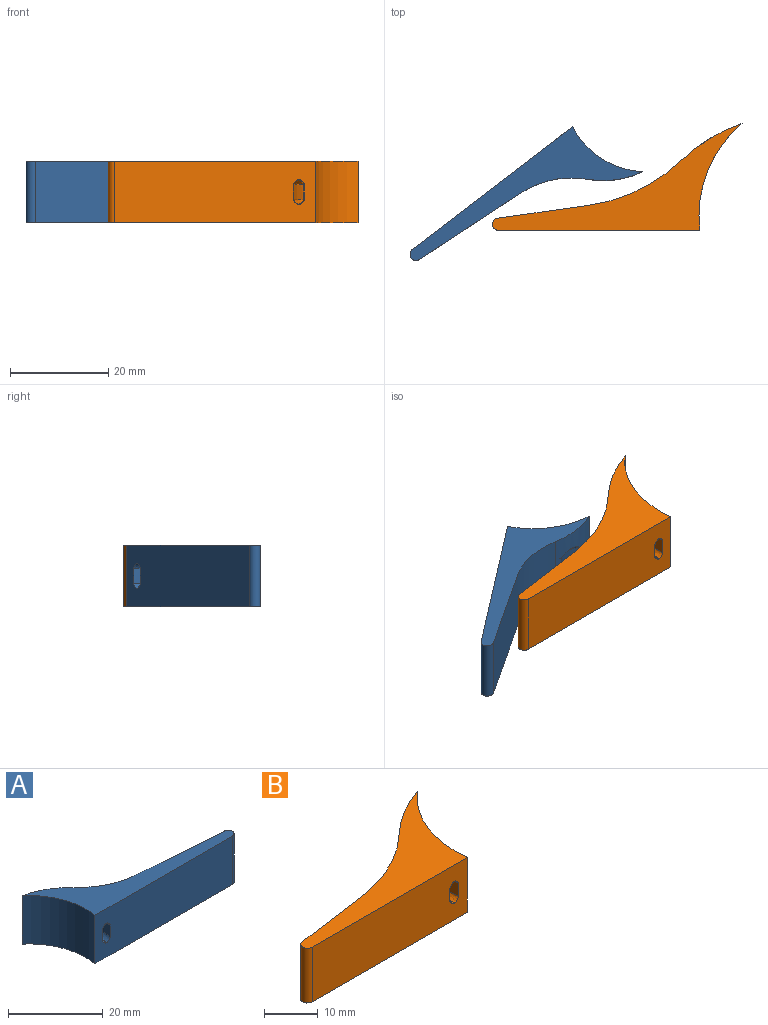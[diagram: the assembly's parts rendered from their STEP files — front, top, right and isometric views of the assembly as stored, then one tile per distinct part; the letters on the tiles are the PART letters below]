
ASSEMBLY  parts=2 mates=1
PART A: 16 faces, bbox 48.3x17.1x12.7 mm
  f0: plane 41.22x12.71mm, normal (0,-1,0), area 502.6mm2, adj f2,f3,f6,f7,f8,f9,f10,f11
  f1: cylinder r=18.88mm len=12.5mm, axis (0,0,1), area 123.5mm2, adj f2,f5,f6,f7,f8,f9,f10,f11
  f2: cylinder r=17mm len=15.97mm, axis (0,0,1), area 222.5mm2, adj f0,f1,f6,f7
  f3: cylinder r=1.24mm len=12.5mm, axis (0,0,1), area 47.6mm2, adj f0,f4,f6,f7
  f4: plane 24.55x12.5mm, normal (0.07,1,0), area 307.7mm2, adj f3,f5,f6,f7
  f5: cylinder r=18.88mm len=12.5mm, axis (0,0,1), area 177.2mm2, adj f1,f4,f6,f7
  f6: plane 48.06x15.97mm, normal (0,0,1), area 228.8mm2, adj f0,f1,f2,f3,f4,f5
  f7: plane 48.06x15.97mm, normal (0,0,-1), area 228.8mm2, adj f0,f1,f2,f3,f4,f5
  f8: plane 13.24x3.15mm, normal (0,0,1), area 3.1mm2, adj f0,f1,f14,f15
  f9: cylinder r=21.47mm len=11.42mm, axis (0,0,-1), area 35mm2, adj f0,f1,f13,f15
  f10: plane 13.24x3.15mm, normal (0,0,-1), area 3.1mm2, adj f0,f1,f12,f13
  f11: cylinder r=19.24mm len=14.35mm, axis (0,0,-1), area 45.5mm2, adj f0,f1,f12,f14
  f12: bspline ~16.52x5.39mm, area 21.4mm2, adj f0,f1,f10,f11
  f13: bspline ~13.54x3.58mm, area 18.7mm2, adj f0,f1,f9,f10
  f14: bspline ~16.52x5.39mm, area 21.4mm2, adj f0,f1,f8,f11
  f15: bspline ~13.54x3.58mm, area 18.7mm2, adj f0,f1,f8,f9
PART B: 16 faces, bbox 51x23.1x12.7 mm
  f0: plane 18.46x12.5mm, normal (-0.14,0.99,0), area 233mm2, adj f1,f5,f6,f7
  f1: cylinder r=1.24mm len=12.5mm, axis (0,0,-1), area 46.6mm2, adj f0,f2,f6,f7
  f2: plane 41.14x12.71mm, normal (0,-1,0), area 501.7mm2, adj f1,f3,f6,f7,f8,f9,f10,f11
  f3: cylinder r=24.5mm len=21.72mm, axis (0,0,-1), area 304.2mm2, adj f2,f4,f6,f7
  f4: cylinder r=34.12mm len=12.5mm, axis (0,0,-1), area 160.4mm2, adj f3,f5,f6,f7,f8,f9,f10,f11
  f5: cylinder r=34.12mm len=18.81mm, axis (0,0,-1), area 265.4mm2, adj f0,f4,f6,f7
  f6: plane 50.74x21.72mm, normal (0,0,1), area 319.7mm2, adj f0,f1,f2,f3,f4,f5
  f7: plane 50.74x21.72mm, normal (0,0,-1), area 319.7mm2, adj f0,f1,f2,f3,f4,f5
  f8: plane 17.94x4.76mm, normal (0,0,1), area 4.3mm2, adj f2,f4,f14,f15
  f9: cylinder r=26.82mm len=19.21mm, axis (0,0,-1), area 61.3mm2, adj f2,f4,f13,f15
  f10: plane 17.94x4.76mm, normal (0,0,-1), area 4.3mm2, adj f2,f4,f12,f13
  f11: cylinder r=29.05mm len=16.14mm, axis (0,0,-1), area 49.9mm2, adj f2,f4,f12,f14
  f12: bspline ~18.22x5.12mm, area 26.1mm2, adj f2,f4,f10,f11
  f13: bspline ~21.81x7.39mm, area 29mm2, adj f2,f4,f9,f10
  f14: bspline ~18.22x5.12mm, area 26.1mm2, adj f2,f4,f8,f11
  f15: bspline ~21.81x7.39mm, area 29mm2, adj f2,f4,f8,f9
PLACE A rot(axis=(0,0,-1),142.5deg) t=(-44.02,11.31,21.97)mm
PLACE B t=(-27.48,18.07,9.47)mm
MATE planar B.f7 <-> A.f7  axis (0,0,-1) through (-3.35,20.83,9.47)mm
